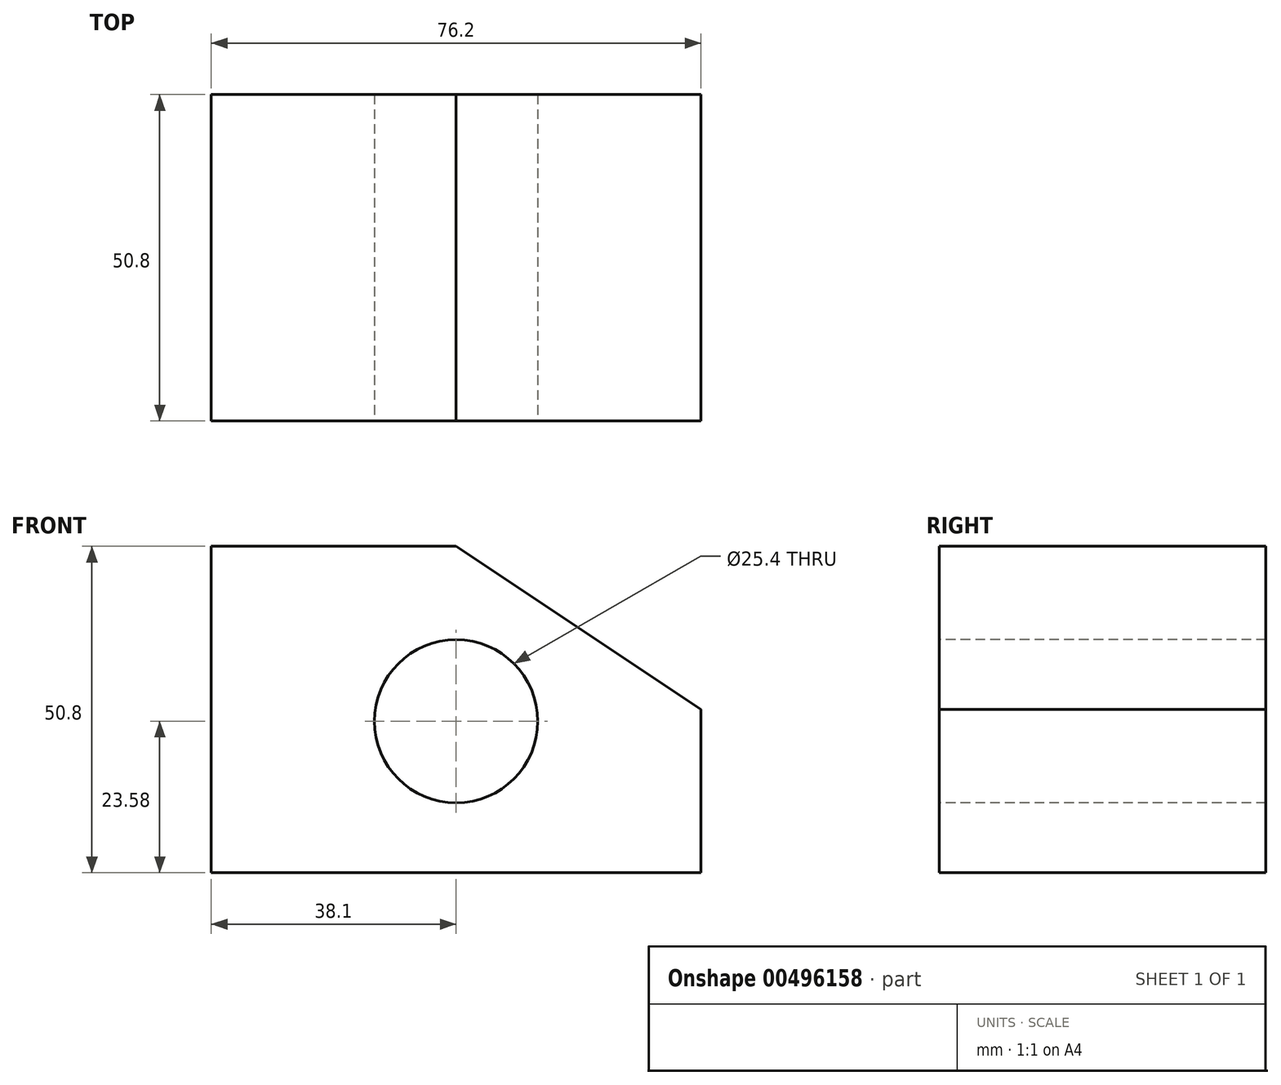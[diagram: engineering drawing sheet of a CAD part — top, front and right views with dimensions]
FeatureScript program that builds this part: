
annotation { "Feature Type Name" : "Feature", "Feature Type Description" : "" }
export const myFeature = defineFeature(function(context is Context, id is Id, definition is map)
    precondition{}
    {
        {
            var Q0;
            Q0=qCreatedBy(makeId("Front.planeOp"),FACE);
            var sketch = newSketch(context, id + "F0", { "sketchPlane" : qUnion([Q0])});
            skLineSegment(sketch, "E0.bottom", {"start": v(0, 0) * mm, "end": v(76.2, 0) * mm});
            skLineSegment(sketch, "E0.top", {"start": v(0, 50.8) * mm, "end": v(38.1, 50.8) * mm});
            skLineSegment(sketch, "E0.left", {"start": v(0, 0) * mm, "end": v(0, 50.8) * mm});
            skLineSegment(sketch, "E0.right", {"start": v(76.2, 0) * mm, "end": v(76.2, 25.4) * mm});
            skLineSegment(sketch, "E1", {"start": v(38.1, 50.8) * mm, "end": v(76.2, 25.4) * mm});
            skPoint(sketch, "E2.orphan", {"position": v(76.2, 50.8) * mm});
            skSolve(sketch);
        }
        {
            var Q0;
            Q0 = qSketchRegion(id + "F0", true);
            extrude(context, id + "F1", {"entities" : qUnion([Q0]), "depth" : 50.8 * mm});
        }
        {
            var Q0;
            Q0=makeQuery(id+"F1.opExtrude","CAP_FACE",FACE,{"disambiguationData":[OSD([sQuery(id+"F0.wireOp",EDGE,"E0.bottom"),sQuery(id+"F0.wireOp",EDGE,"E0.top"),sQuery(id+"F0.wireOp",EDGE,"E0.left"),sQuery(id+"F0.wireOp",EDGE,"E0.right"),sQuery(id+"F0.wireOp",EDGE,"E1")])],"isStart":false});
            var sketch = newSketch(context, id + "F2", { "sketchPlane" : qUnion([Q0])});
            skCircle(sketch, "E3", {"center": v(38.1, 23.58) * mm, "radius": 12.7 * mm});
            skSolve(sketch);
        }
        {
            var Q0;
            Q0=makeQuery(id+"F2.imprint","IMPRINT",FACE,{"disambiguationData":[TD([[makeQuery(id+"F2.imprint","IMPRINT",EDGE,{"derivedFrom":sQuery(id+"F2.wireOp",EDGE,"E3")}),1.0]])]});
            extrude(context, id + "F3", {"entities" : qUnion([Q0]), "operationType" : NewBodyOperationType.REMOVE, "oppositeDirection" : true, "depth" : 76.2 * mm});
        }
    });
